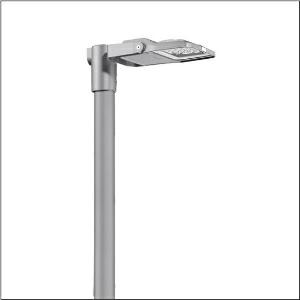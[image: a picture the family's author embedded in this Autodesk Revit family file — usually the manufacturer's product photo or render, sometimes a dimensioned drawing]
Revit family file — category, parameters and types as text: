
# Revit family: floodlight_fl_21_iq_micro___pl52_5xa7762a4d3a_1d61
name_source: partatom
category: Lighting Fixtures
units: mm (PartAtom-declared; Revit-internal decimal feet)

## family parameters
Cut with Voids When Loaded = No
Host = Face
Light Source = No
Part Type = Normal
Room Calculation Point = No
Round Connector Dimension = Use Diameter
Shared = No

## types (1)
- --- (1 x LED, 3010 lm, 23.1 W, 4000K)
    Apparent Load = 23 VA
    CIE Flux Codes = 26 60 98 100 100
    Color Rendering = 70
    Color Temperature = 4000K
    Default Elevation = 1800 mm
    Description = Floodlight FL 21 iQ micro, floodlight, primary light control with lens, of PMMA, primary optical cover: protective disc, of toughened safety glass, transparent, light distribution: PL52, light emission: direct distribution, installation type: surface-mounted, LED, High Power LED, rated luminous flux: 3.010lm, luminous efficacy: 130lm/W, light colour: 740, colour temperature: 4000K, control: Auto-Match, Temp-Guard, Night-Set, Smart-Wire, Desk-Remote (wireless, voltage-free reading and setting of iQ features in the workshop via application-optimized NFC function/RFID function), optimised constant luminous flux control (CLO 2.0), Street-Remote, with terminal, 6-pole, mains connection: 220..240V, AC, 50/60Hz, start of lifetime: 23W, end of service life: 24W, reduction: 11W, luminaire housing, of diecast aluminium, powder-coated, Siteco® metallic grey (DB 702S), corrosivity category C5 mid according to DIN EN ISO 12944, sealing non-destructively replaceable, please order mast flange separately, mast bracket, of steel, galvanised, powder-coated, Siteco® metallic grey (DB 702S), protection rating (complete): IP66, insulation class (complete): insulation class II (safety insulation), certification: CE, ENEC, VDE, protection symbol: D, impact resistance: IK07, permissible operating ambient temperature: -40..+40°C, permissible operating ambient temperature for outdoor applications: -40..+50°C, standard: DIN EN 12944, LABS conformity tested according to VDMA 24364:2018-05, packaging unit: 1 piece

Light Distribution: PL52
    Height = 65 mm
    Lamp = 1 x LED
    Lamp Light Flux = 3010 lm
    Lamp Power = 23.1 W
    Lamp count = 1
    Length = 312 mm
    Luminous efficacy = 130 lm/W
    Manufacturer = Siteco
    ModVariant = No
    Model = 5XA7762A4D3A
    Number of Poles = 1
    OnlyDefault = Yes
    Power Factor = 1
    Product Name = Floodlight FL 21 iQ micro | PL52
    Product group = floodlight | pylon annexe
    ProductGroupID = 6200
    Protection Class = Protection class II
    Protection Degree = IP 66
    RLX_Detail_Level = 1
    RLX_Emergency_Light_Flux = 0 lm
    RLX_Emergency_Type = 0
    RLX_Emergency_Type_DB = No
    RlxData = <blob elided: 102017 chars, md5=68a78ea2>
    Socket = socket
    Standby Power = 0 W
    System Light Flux = 3010 lm
    System Power = 23 W
    Type Comments = factory setting: luminous flux: 100 % | dim-lin: 254 | 455 mA
    Type Image = l_1007121.jpg
    URL = http://relux.com
    VarID = @adj_149023
    Voltage = 0 V
    Weight = 0.00 kg
    Width = 230 mm

## geometry (parser evidence)
native form markers: Blend x4, Sweep x12
no freeform markers — native parametric forms only
